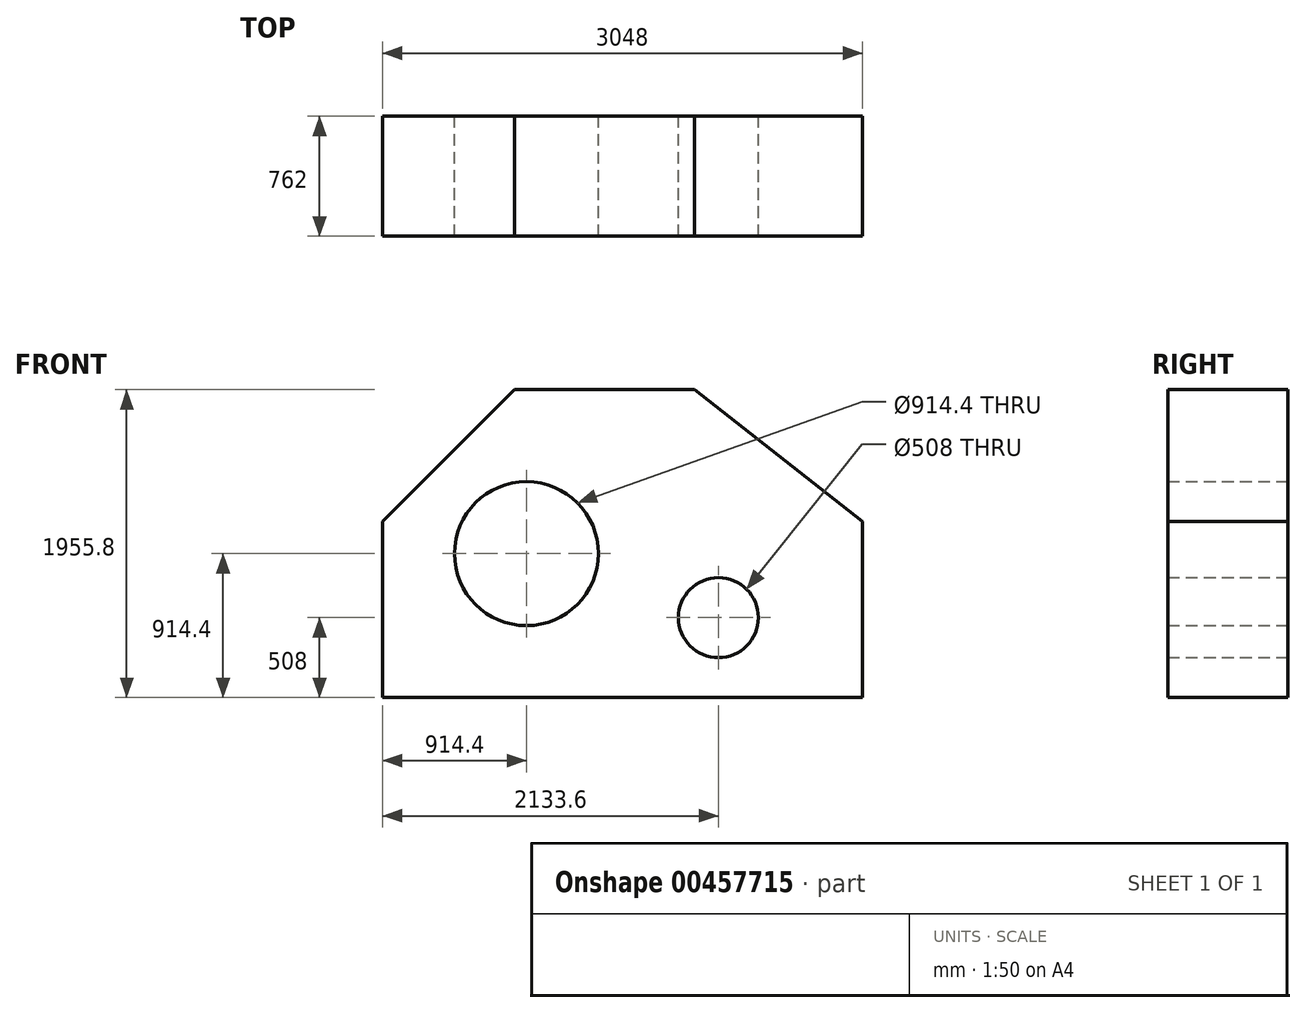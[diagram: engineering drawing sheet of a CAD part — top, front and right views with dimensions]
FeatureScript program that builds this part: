
annotation { "Feature Type Name" : "Feature", "Feature Type Description" : "" }
export const myFeature = defineFeature(function(context is Context, id is Id, definition is map)
    precondition{}
    {
        {
            var Q0;
            Q0=qCreatedBy(makeId("Front.planeOp"),FACE);
            var sketch = newSketch(context, id + "F0", { "sketchPlane" : qUnion([Q0])});
            skLineSegment(sketch, "E0", {"start": v(0, 0) * mm, "end": v(3048, 0) * mm});
            skLineSegment(sketch, "E1", {"start": v(3048, 0) * mm, "end": v(3048, 1117.6) * mm});
            skLineSegment(sketch, "E2", {"start": v(0, 0) * mm, "end": v(0, 1117.6) * mm});
            skLineSegment(sketch, "E3", {"start": v(838.2, 1955.8) * mm, "end": v(1981.2, 1955.8) * mm});
            skLineSegment(sketch, "E4", {"start": v(0, 1117.6) * mm, "end": v(838.2, 1955.8) * mm});
            skLineSegment(sketch, "E5", {"start": v(3048, 1117.6) * mm, "end": v(1981.2, 1955.8) * mm});
            skCircle(sketch, "E6", {"center": v(914.4, 914.4) * mm, "radius": 457.2 * mm});
            skCircle(sketch, "E7", {"center": v(2133.6, 508) * mm, "radius": 254 * mm});
            skSolve(sketch);
        }
        {
            var Q0;
            Q0 = qSketchRegion(id + "F0", true);
            extrude(context, id + "F1", {"entities" : qUnion([Q0]), "depth" : 762 * mm});
        }
    });
